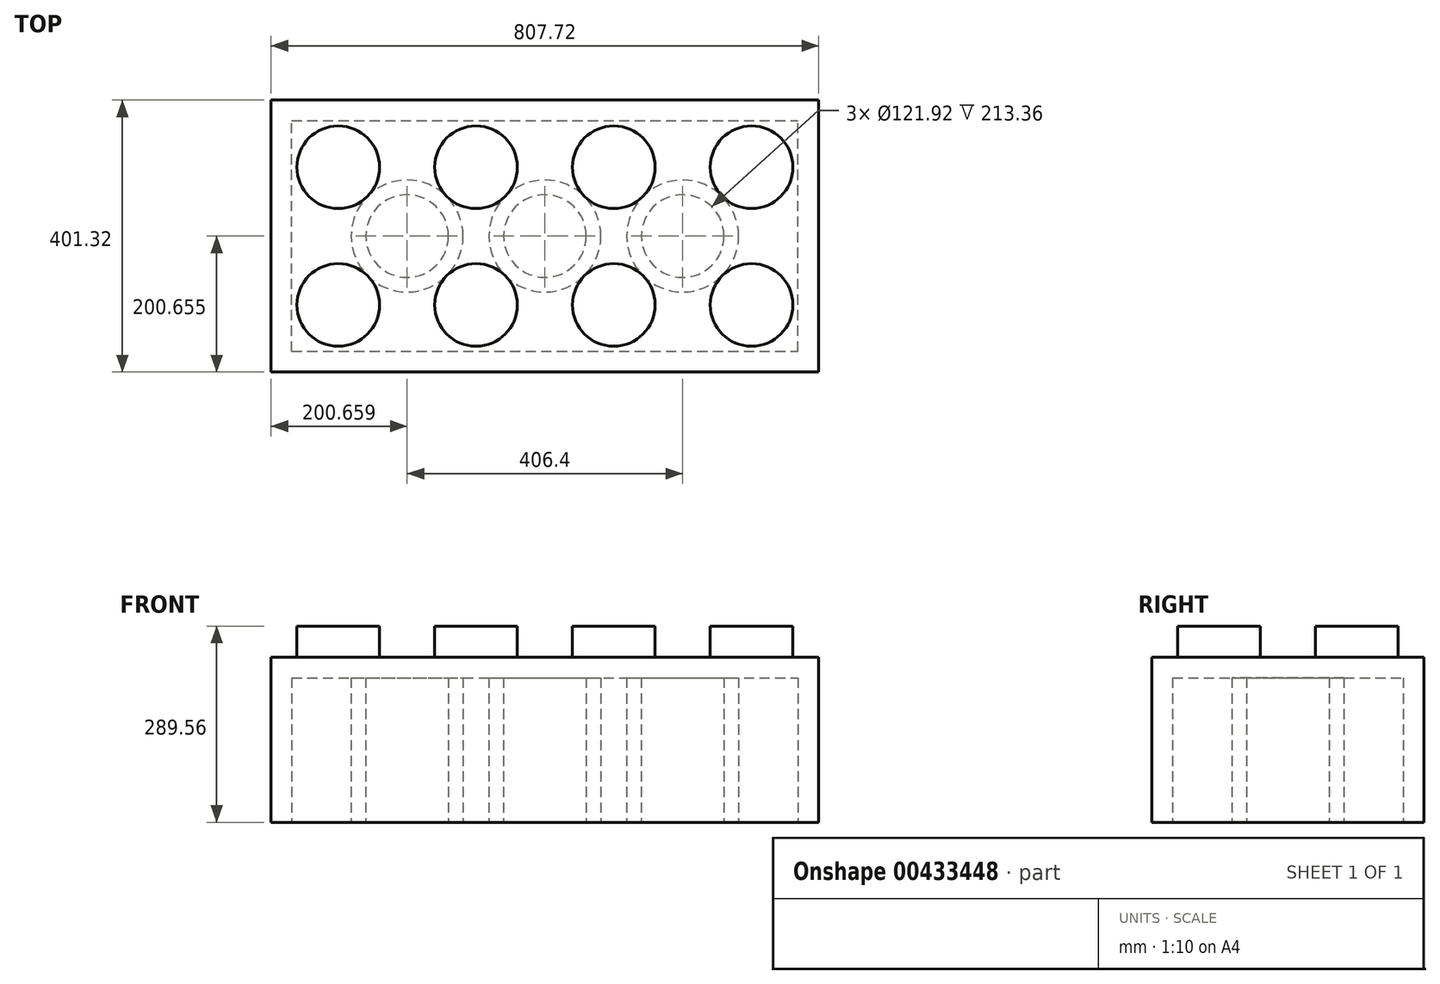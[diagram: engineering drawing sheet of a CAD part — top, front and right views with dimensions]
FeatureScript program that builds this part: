
annotation { "Feature Type Name" : "Feature", "Feature Type Description" : "" }
export const myFeature = defineFeature(function(context is Context, id is Id, definition is map)
    precondition{}
    {
        {
            var Q0;
            Q0=qCreatedBy(makeId("Top.planeOp"),FACE);
            var sketch = newSketch(context, id + "F0", { "sketchPlane" : qUnion([Q0])});
            skLineSegment(sketch, "E0.bottom", {"start": v(-413.21, 183.95) * mm, "end": v(394.5, 183.95) * mm});
            skLineSegment(sketch, "E0.top", {"start": v(-413.21, -217.37) * mm, "end": v(394.5, -217.37) * mm});
            skLineSegment(sketch, "E0.left", {"start": v(-413.21, 183.95) * mm, "end": v(-413.21, -217.37) * mm});
            skLineSegment(sketch, "E0.right", {"start": v(394.5, 183.95) * mm, "end": v(394.5, -217.37) * mm});
            skSolve(sketch);
        }
        {
            var Q0;
            Q0=makeQuery(id+"F0.imprint","IMPRINT",FACE,{"disambiguationData":[TD([[makeQuery(id+"F0.imprint","IMPRINT",EDGE,{"derivedFrom":sQuery(id+"F0.wireOp",EDGE,"E0.bottom")}),-1.0]])]});
            extrude(context, id + "F1", {"entities" : qUnion([Q0]), "depth" : 243.84 * mm});
        }
        {
            var Q0;
            Q0=makeQuery(id+"F1.opExtrude","CAP_FACE",FACE,{"disambiguationData":[OSD([sQuery(id+"F0.wireOp",EDGE,"E0.bottom"),sQuery(id+"F0.wireOp",EDGE,"E0.top"),sQuery(id+"F0.wireOp",EDGE,"E0.left"),sQuery(id+"F0.wireOp",EDGE,"E0.right")])],"isStart":false});
            var sketch = newSketch(context, id + "F2", { "sketchPlane" : qUnion([Q0])});
            skCircle(sketch, "E1", {"center": v(-314.15, 84.89) * mm, "radius": 60.96 * mm});
            skCircle(sketch, "E2.0.1.0", {"center": v(-314.15, -118.31) * mm, "radius": 60.96 * mm});
            skCircle(sketch, "E2.1.0.0", {"center": v(-110.95, 84.89) * mm, "radius": 60.96 * mm});
            skCircle(sketch, "E2.1.1.0", {"center": v(-110.95, -118.31) * mm, "radius": 60.96 * mm});
            skCircle(sketch, "E2.2.0.0", {"center": v(92.25, 84.89) * mm, "radius": 60.96 * mm});
            skCircle(sketch, "E2.2.1.0", {"center": v(92.25, -118.31) * mm, "radius": 60.96 * mm});
            skCircle(sketch, "E2.3.0.0", {"center": v(295.45, 84.89) * mm, "radius": 60.96 * mm});
            skCircle(sketch, "E2.3.1.0", {"center": v(295.45, -118.31) * mm, "radius": 60.96 * mm});
            skLineSegment(sketch, "E2.direction1", {"start": v(-314.15, 84.89) * mm, "end": v(-110.95, 84.89) * mm, "construction": true});
            skLineSegment(sketch, "E2.direction2", {"start": v(-314.15, 84.89) * mm, "end": v(-314.15, -118.31) * mm, "construction": true});
            skSolve(sketch);
        }
        {
            var Q0;
            Q0=makeQuery(id+"F2.imprint","IMPRINT",FACE,{"disambiguationData":[TD([[makeQuery(id+"F2.imprint","IMPRINT",EDGE,{"derivedFrom":sQuery(id+"F2.wireOp",EDGE,"E1")}),1.0]])]});
            var Q1;
            Q1=makeQuery(id+"F2.imprint","IMPRINT",FACE,{"disambiguationData":[TD([[makeQuery(id+"F2.imprint","IMPRINT",EDGE,{"derivedFrom":sQuery(id+"F2.wireOp",EDGE,"E2.0.1.0")}),1.0]])]});
            var Q2;
            Q2=makeQuery(id+"F2.imprint","IMPRINT",FACE,{"disambiguationData":[TD([[makeQuery(id+"F2.imprint","IMPRINT",EDGE,{"derivedFrom":sQuery(id+"F2.wireOp",EDGE,"E2.1.0.0")}),1.0]])]});
            var Q3;
            Q3=makeQuery(id+"F2.imprint","IMPRINT",FACE,{"disambiguationData":[TD([[makeQuery(id+"F2.imprint","IMPRINT",EDGE,{"derivedFrom":sQuery(id+"F2.wireOp",EDGE,"E2.2.0.0")}),1.0]])]});
            var Q4;
            Q4=makeQuery(id+"F2.imprint","IMPRINT",FACE,{"disambiguationData":[TD([[makeQuery(id+"F2.imprint","IMPRINT",EDGE,{"derivedFrom":sQuery(id+"F2.wireOp",EDGE,"E2.2.1.0")}),1.0]])]});
            var Q5;
            Q5=makeQuery(id+"F2.imprint","IMPRINT",FACE,{"disambiguationData":[TD([[makeQuery(id+"F2.imprint","IMPRINT",EDGE,{"derivedFrom":sQuery(id+"F2.wireOp",EDGE,"E2.1.1.0")}),1.0]])]});
            var Q6;
            Q6=makeQuery(id+"F2.imprint","IMPRINT",FACE,{"disambiguationData":[TD([[makeQuery(id+"F2.imprint","IMPRINT",EDGE,{"derivedFrom":sQuery(id+"F2.wireOp",EDGE,"E2.3.0.0")}),1.0]])]});
            var Q7;
            Q7=makeQuery(id+"F2.imprint","IMPRINT",FACE,{"disambiguationData":[TD([[makeQuery(id+"F2.imprint","IMPRINT",EDGE,{"derivedFrom":sQuery(id+"F2.wireOp",EDGE,"E2.3.1.0")}),1.0]])]});
            extrude(context, id + "F3", {"entities" : qUnion([Q0, Q1, Q2, Q3, Q4, Q5, Q6, Q7]), "operationType" : NewBodyOperationType.ADD, "depth" : 45.72 * mm});
        }
        {
            var Q0;
            Q0=makeQuery(id+"F1.opExtrude","CAP_FACE",FACE,{"disambiguationData":[OSD([sQuery(id+"F0.wireOp",EDGE,"E0.bottom"),sQuery(id+"F0.wireOp",EDGE,"E0.top"),sQuery(id+"F0.wireOp",EDGE,"E0.left"),sQuery(id+"F0.wireOp",EDGE,"E0.right")])],"isStart":true});
            var sketch = newSketch(context, id + "F4", { "sketchPlane" : qUnion([Q0])});
            skLineSegment(sketch, "E3.bottom", {"start": v(-382.73, 186.9) * mm, "end": v(364.03, 186.9) * mm});
            skLineSegment(sketch, "E3.top", {"start": v(-382.73, -153.47) * mm, "end": v(364.03, -153.47) * mm});
            skLineSegment(sketch, "E3.left", {"start": v(-382.73, 186.9) * mm, "end": v(-382.73, -153.47) * mm});
            skLineSegment(sketch, "E3.right", {"start": v(364.03, 186.9) * mm, "end": v(364.03, -153.47) * mm});
            skCircle(sketch, "E4", {"center": v(-212.55, 16.71) * mm, "radius": 82.55 * mm});
            skCircle(sketch, "E5", {"center": v(-212.55, 16.71) * mm, "radius": 60.96 * mm});
            skCircle(sketch, "E6.1.0.0", {"center": v(-9.35, 16.71) * mm, "radius": 60.96 * mm});
            skCircle(sketch, "E6.1.0.1", {"center": v(-9.35, 16.71) * mm, "radius": 82.55 * mm});
            skCircle(sketch, "E6.2.0.0", {"center": v(193.85, 16.71) * mm, "radius": 60.96 * mm});
            skCircle(sketch, "E6.2.0.1", {"center": v(193.85, 16.71) * mm, "radius": 82.55 * mm});
            skLineSegment(sketch, "E6.direction1", {"start": v(-212.55, 16.71) * mm, "end": v(-9.35, 16.71) * mm, "construction": true});
            skSolve(sketch);
        }
        {
            var Q0;
            Q0=makeQuery(id+"F4.imprint","IMPRINT",FACE,{"disambiguationData":[TD([[makeQuery(id+"F4.imprint","IMPRINT",EDGE,{"derivedFrom":sQuery(id+"F4.wireOp",EDGE,"E3.bottom")}),-1.0]])]});
            var Q1;
            Q1=makeQuery(id+"F4.imprint","IMPRINT",FACE,{"disambiguationData":[TD([[makeQuery(id+"F4.imprint","IMPRINT",EDGE,{"derivedFrom":sQuery(id+"F4.wireOp",EDGE,"E5")}),1.0]])]});
            var Q2;
            Q2=makeQuery(id+"F4.imprint","IMPRINT",FACE,{"disambiguationData":[TD([[makeQuery(id+"F4.imprint","IMPRINT",EDGE,{"derivedFrom":sQuery(id+"F4.wireOp",EDGE,"E6.1.0.0")}),1.0]])]});
            var Q3;
            Q3=makeQuery(id+"F4.imprint","IMPRINT",FACE,{"disambiguationData":[TD([[makeQuery(id+"F4.imprint","IMPRINT",EDGE,{"derivedFrom":sQuery(id+"F4.wireOp",EDGE,"E6.2.0.0")}),1.0]])]});
            extrude(context, id + "F5", {"entities" : qUnion([Q0, Q1, Q2, Q3]), "operationType" : NewBodyOperationType.REMOVE, "oppositeDirection" : true, "depth" : 213.36 * mm});
        }
    });
